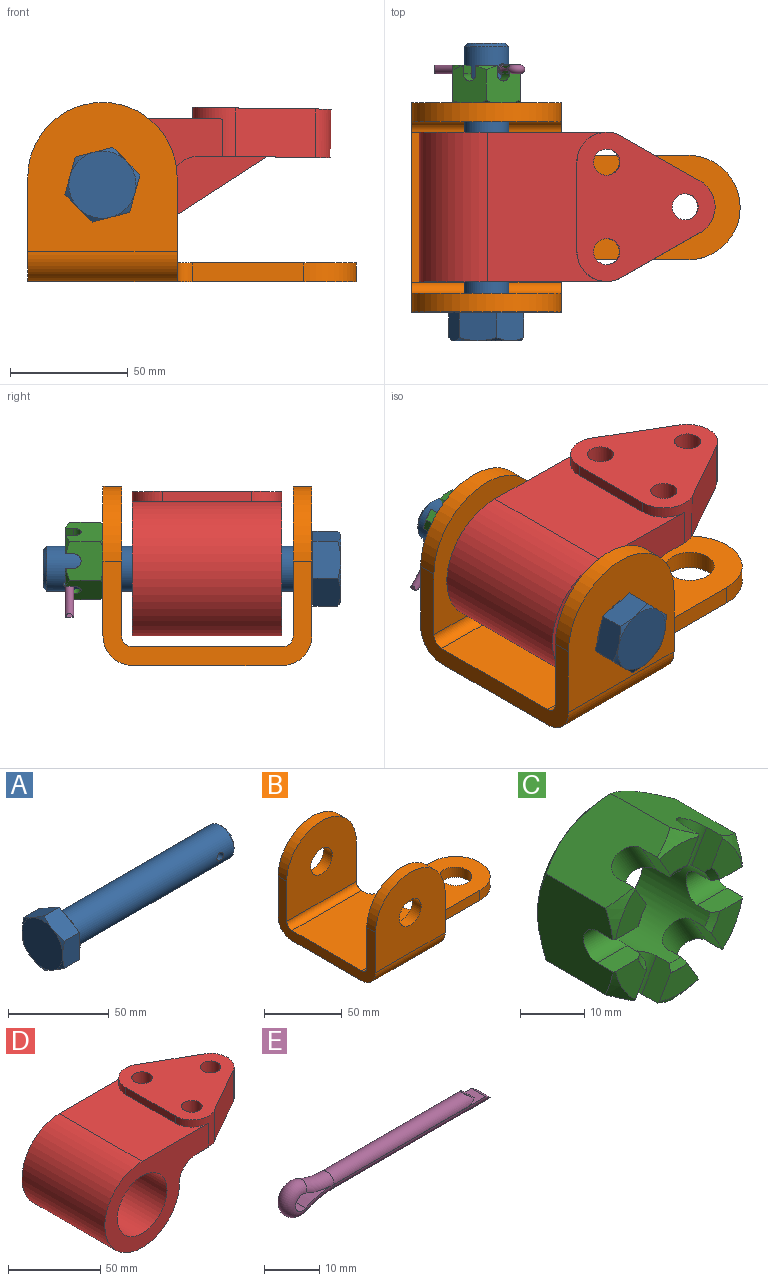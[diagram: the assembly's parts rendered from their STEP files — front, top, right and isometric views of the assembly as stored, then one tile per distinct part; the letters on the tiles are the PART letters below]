
ASSEMBLY  parts=5 mates=4
PART A: 26 faces, bbox 126.6x33x33 mm
  f0: plane 28.58x28.58mm, normal (1,0,0), area 325.1mm2, adj f10,f24
  f1: cylinder r=9.53mm len=112.28mm, axis (-1,0,0), area 6683.8mm2, adj f2,f24,f25
  f2: cone r=8.01mm half-angle=45deg, axis (-1,0,0), area 117.9mm2, adj f1,f3
  f3: plane 16.03x16.03mm, normal (1,0,0), area 201.7mm2, adj f2
  f4: plane 12.37x7.14mm, normal (1,0,0), area 11mm2, adj f10,f18,f23
  f5: plane 14.29x4.12mm, normal (1,0,0), area 11mm2, adj f10,f22,f23
  f6: plane 12.37x7.14mm, normal (1,0,0), area 11mm2, adj f10,f21,f22
  f7: plane 12.37x7.14mm, normal (1,0,0), area 11mm2, adj f10,f20,f21
  f8: plane 14.29x4.12mm, normal (1,0,0), area 11mm2, adj f10,f19,f20
  f9: plane 12.37x7.14mm, normal (1,0,0), area 11mm2, adj f10,f18,f19
  f10: cylinder r=14.29mm len=28.58mm, axis (-1,0,0), area 34.2mm2, adj f0,f4,f5,f6,f7,f8,f9
  f11: plane 28.58x28.58mm, normal (-1,0,0), area 641.3mm2, adj f12,f13,f14,f15,f16,f17
  f12: cone r=14.29mm half-angle=60deg, axis (1,0,0), area 12.7mm2, adj f11,f22,f23
  f13: cone r=14.29mm half-angle=60deg, axis (1,0,0), area 12.7mm2, adj f11,f21,f22
  f14: cone r=14.29mm half-angle=60deg, axis (1,0,0), area 12.7mm2, adj f11,f20,f21
  f15: cone r=14.29mm half-angle=60deg, axis (1,0,0), area 12.7mm2, adj f11,f19,f20
  f16: cone r=14.29mm half-angle=60deg, axis (1,0,0), area 12.7mm2, adj f11,f18,f23
  f17: cone r=14.29mm half-angle=60deg, axis (1,0,0), area 12.7mm2, adj f11,f18,f19
  f18: plane 16.51x11.89mm, normal (0,1,0), area 188.9mm2, adj f4,f9,f16,f17,f19,f23
  f19: plane 14.29x11.89mm, normal (0,0.5,-0.87), area 188.9mm2, adj f8,f9,f15,f17,f18,f20
  f20: plane 14.29x11.89mm, normal (0,-0.5,-0.87), area 188.9mm2, adj f7,f8,f14,f15,f19,f21
  f21: plane 16.51x11.89mm, normal (0,-1,0), area 188.9mm2, adj f6,f7,f13,f14,f20,f22
  f22: plane 14.29x11.89mm, normal (0,-0.5,0.87), area 188.9mm2, adj f5,f6,f12,f13,f21,f23
  f23: plane 14.29x11.89mm, normal (0,0.5,0.87), area 188.9mm2, adj f4,f5,f12,f16,f18,f22
  f24: torus R=10.03mm, axis (1,0,0), area 48.7mm2, adj f0,f1
  f25: cylinder r=2.38mm len=19.05mm, axis (0,-1,0), area 285mm2, adj f1
PART B: 24 faces, bbox 139.7x88.9x76.2 mm
  f0: plane 63.5x63.5mm, normal (0,-1,0), area 3290.3mm2, adj f5,f8,f16,f18,f23
  f1: plane 139.7x63.5mm, normal (0,0,1), area 6554.8mm2, adj f5,f6,f8,f9,f10,f11,f12,f13
  f2: plane 63.5x63.5mm, normal (0,1,0), area 3290.3mm2, adj f6,f8,f17,f19,f22
  f3: plane 63.5x63.5mm, normal (0,1,0), area 3290.3mm2, adj f5,f8,f16,f18,f21
  f4: plane 63.5x63.5mm, normal (0,-1,0), area 3290.3mm2, adj f6,f8,f17,f19,f20
  f5: plane 44.45x15.88mm, normal (1,0,0), area 386.1mm2, adj f0,f1,f3,f7,f12,f16,f21,f23
  f6: plane 44.45x15.88mm, normal (1,0,0), area 386.1mm2, adj f1,f2,f4,f7,f15,f17,f20,f22
  f7: plane 139.7x63.5mm, normal (0,0,-1), area 6554.8mm2, adj f5,f6,f8,f9,f10,f11,f12,f13
  f8: plane 88.9x44.45mm, normal (-1,0,0), area 1225.8mm2, adj f0,f1,f2,f3,f4,f7,f16,f17
  f9: plane 47.63x7.94mm, normal (0,-1,0), area 378mm2, adj f1,f7,f10,f15
  f10: cylinder r=22.23mm len=44.45mm, axis (0,0,-1), area 554.2mm2, adj f1,f7,f9,f11
  f11: plane 47.63x7.94mm, normal (0,1,0), area 378mm2, adj f1,f7,f10,f12
  f12: cylinder r=6.35mm len=7.94mm, axis (0,0,-1), area 79.2mm2, adj f1,f5,f7,f11
  f13: cylinder r=10.33mm len=20.65mm, axis (0,0,-1), area 514.9mm2, adj f1,f7
  f14: cylinder r=10.33mm len=20.65mm, axis (0,0,-1), area 514.9mm2, adj f1,f7
  f15: cylinder r=6.35mm len=7.94mm, axis (0,0,-1), area 79.2mm2, adj f1,f6,f7,f9
  f16: cylinder r=31.75mm len=63.5mm, axis (0,-1,0), area 791.7mm2, adj f0,f3,f5,f8
  f17: cylinder r=31.75mm len=63.5mm, axis (0,-1,0), area 791.7mm2, adj f2,f4,f6,f8
  f18: cylinder r=9.92mm len=19.85mm, axis (0,-1,0), area 494.9mm2, adj f0,f3
  f19: cylinder r=9.92mm len=19.85mm, axis (0,-1,0), area 494.9mm2, adj f2,f4
  f20: cylinder r=12.7mm len=63.5mm, axis (-1,0,0), area 1266.8mm2, adj f4,f6,f7,f8
  f21: cylinder r=12.7mm len=63.5mm, axis (-1,0,0), area 1266.8mm2, adj f3,f5,f7,f8
  f22: cylinder r=4.76mm len=63.5mm, axis (-1,0,0), area 475mm2, adj f1,f2,f6,f8
  f23: cylinder r=4.76mm len=63.5mm, axis (-1,0,0), area 475mm2, adj f0,f1,f5,f8
PART C: 64 faces, bbox 33x16.9x33 mm
  f0: cylinder r=8.33mm len=16.67mm, axis (0,-1,0), area 599.6mm2, adj f8,f9,f10,f11,f12,f13,f14,f15
  f1: plane 28.58x28.58mm, normal (0,1,0), area 356.3mm2, adj f32,f33,f34,f35,f36,f37,f51
  f2: plane 8.68x4.95mm, normal (0,-1,0), area 30mm2, adj f12,f16,f41,f48
  f3: plane 7.52x6.81mm, normal (0,-1,0), area 30mm2, adj f9,f13,f43,f49
  f4: plane 7.52x6.81mm, normal (0,-1,0), area 30mm2, adj f8,f18,f39,f44
  f5: plane 7.52x6.81mm, normal (0,-1,0), area 30mm2, adj f11,f15,f42,f46
  f6: plane 7.52x6.81mm, normal (0,-1,0), area 30mm2, adj f10,f17,f40,f47
  f7: plane 8.68x4.95mm, normal (0,-1,0), area 30mm2, adj f14,f19,f38,f45
  f8: plane 6.56x3.71mm, normal (0,0,-1), area 23.4mm2, adj f0,f4,f22,f26,f39,f44,f62,f63
  f9: plane 6.56x3.71mm, normal (0,0,1), area 23.4mm2, adj f0,f3,f22,f26,f43,f49,f52,f53
  f10: plane 6.56x3.71mm, normal (0,0,1), area 23.4mm2, adj f0,f6,f25,f27,f40,f47,f56,f57
  f11: plane 6.56x3.71mm, normal (0,0,-1), area 23.4mm2, adj f0,f5,f25,f27,f42,f46,f58,f59
  f12: plane 5.69x3.71mm, normal (0.87,0,0.5), area 23.4mm2, adj f0,f2,f23,f28,f41,f48,f54,f55
  f13: plane 5.69x3.71mm, normal (-0.87,0,-0.5), area 23.4mm2, adj f0,f3,f23,f28,f43,f49,f52,f53
  f14: plane 5.69x3.71mm, normal (-0.87,0,-0.5), area 23.4mm2, adj f0,f7,f20,f29,f38,f45,f60,f61
  f15: plane 5.69x3.71mm, normal (0.87,0,0.5), area 23.4mm2, adj f0,f5,f20,f29,f42,f46,f58,f59
  f16: plane 5.69x3.71mm, normal (-0.87,0,0.5), area 23.4mm2, adj f0,f2,f24,f30,f41,f48,f54,f55
  f17: plane 5.69x3.71mm, normal (0.87,0,-0.5), area 23.4mm2, adj f0,f6,f24,f30,f40,f47,f56,f57
  f18: plane 5.69x3.71mm, normal (-0.87,0,0.5), area 23.4mm2, adj f0,f4,f21,f31,f39,f44,f62,f63
  f19: plane 5.69x3.71mm, normal (0.87,0,-0.5), area 23.4mm2, adj f0,f7,f21,f31,f38,f45,f60,f61
  f20: plane 16.62x14.29mm, normal (-0.5,0,0.87), area 220.6mm2, adj f14,f15,f21,f25,f29,f32,f33,f38
  f21: plane 16.62x14.29mm, normal (0.5,0,0.87), area 220.6mm2, adj f18,f19,f20,f22,f31,f33,f34,f38
  f22: plane 16.63x16.51mm, normal (1,0,0), area 220.6mm2, adj f8,f9,f21,f23,f26,f34,f35,f39
  f23: plane 16.62x14.29mm, normal (0.5,0,-0.87), area 220.6mm2, adj f12,f13,f22,f24,f28,f35,f36,f41
  f24: plane 16.62x14.29mm, normal (-0.5,0,-0.87), area 220.6mm2, adj f16,f17,f23,f25,f30,f36,f37,f40
  f25: plane 16.63x16.51mm, normal (-1,0,0), area 220.6mm2, adj f10,f11,f20,f24,f27,f32,f37,f40
  f26: cylinder r=3.05mm len=6.53mm, axis (1,0,0), area 59.8mm2, adj f0,f8,f9,f22
  f27: cylinder r=3.05mm len=6.53mm, axis (1,0,0), area 59.8mm2, adj f0,f10,f11,f25
  f28: cylinder r=3.05mm len=8.7mm, axis (-0.5,0,0.87), area 59.8mm2, adj f0,f12,f13,f23
  f29: cylinder r=3.05mm len=8.7mm, axis (-0.5,0,0.87), area 59.8mm2, adj f0,f14,f15,f20
  f30: cylinder r=3.05mm len=8.7mm, axis (0.5,0,0.87), area 59.8mm2, adj f0,f16,f17,f24
  f31: cylinder r=3.05mm len=8.7mm, axis (0.5,0,0.87), area 59.8mm2, adj f0,f18,f19,f21
  f32: cone r=14.29mm half-angle=49.2deg, axis (0,-1,0), area 14.5mm2, adj f1,f20,f25
  f33: cone r=14.29mm half-angle=49.2deg, axis (0,-1,0), area 14.5mm2, adj f1,f20,f21
  f34: cone r=14.29mm half-angle=49.2deg, axis (0,-1,0), area 14.5mm2, adj f1,f21,f22
  f35: cone r=14.29mm half-angle=49.2deg, axis (0,-1,0), area 14.5mm2, adj f1,f22,f23
  f36: cone r=14.29mm half-angle=49.2deg, axis (0,-1,0), area 14.5mm2, adj f1,f23,f24
  f37: cone r=14.29mm half-angle=49.2deg, axis (0,-1,0), area 14.5mm2, adj f1,f24,f25
  f38: cone r=14.29mm half-angle=49.2deg, axis (0,1,0), area 13.6mm2, adj f7,f14,f19,f20,f21
  f39: cone r=14.29mm half-angle=49.2deg, axis (0,1,0), area 13.6mm2, adj f4,f8,f18,f21,f22
  f40: cone r=14.29mm half-angle=49.2deg, axis (0,1,0), area 13.6mm2, adj f6,f10,f17,f24,f25
  f41: cone r=14.29mm half-angle=49.2deg, axis (0,1,0), area 13.6mm2, adj f2,f12,f16,f23,f24
  f42: cone r=14.29mm half-angle=49.2deg, axis (0,1,0), area 13.6mm2, adj f5,f11,f15,f20,f25
  f43: cone r=14.29mm half-angle=49.2deg, axis (0,1,0), area 13.6mm2, adj f3,f9,f13,f22,f23
  f44: cone r=8.21mm half-angle=55deg, axis (0,-1,0), area 0.1mm2, adj f4,f8,f18,f63
  f45: cone r=8.21mm half-angle=55deg, axis (0,-1,0), area 0.1mm2, adj f7,f14,f19,f60
  f46: cone r=8.21mm half-angle=55deg, axis (0,-1,0), area 0.1mm2, adj f5,f11,f15,f58
  f47: cone r=8.21mm half-angle=55deg, axis (0,-1,0), area 0.1mm2, adj f6,f10,f17,f56
  f48: cone r=8.21mm half-angle=55deg, axis (0,-1,0), area 0.1mm2, adj f2,f12,f16,f54
  f49: cone r=8.21mm half-angle=55deg, axis (0,-1,0), area 0.1mm2, adj f3,f9,f13,f52
  f50: cone r=9.53mm half-angle=55deg, axis (0,1,0), area 81.6mm2, adj f0,f51
  f51: cylinder r=9.53mm len=19.05mm, axis (0,-1,0), area 1.5mm2, adj f1,f50
  f52: cone r=9.53mm half-angle=55deg, axis (0,1,0), area 0.1mm2, adj f9,f13,f49,f53
  f53: cone r=8.33mm half-angle=55deg, axis (0,-1,0), area 4.5mm2, adj f0,f9,f13,f52
  f54: cone r=9.53mm half-angle=55deg, axis (0,1,0), area 0.1mm2, adj f12,f16,f48,f55
  f55: cone r=8.33mm half-angle=55deg, axis (0,-1,0), area 4.5mm2, adj f0,f12,f16,f54
  f56: cone r=9.53mm half-angle=55deg, axis (0,1,0), area 0.1mm2, adj f10,f17,f47,f57
  f57: cone r=8.33mm half-angle=55deg, axis (0,-1,0), area 4.5mm2, adj f0,f10,f17,f56
  f58: cone r=9.53mm half-angle=55deg, axis (0,1,0), area 0.1mm2, adj f11,f15,f46,f59
  f59: cone r=8.33mm half-angle=55deg, axis (0,-1,0), area 4.5mm2, adj f0,f11,f15,f58
  f60: cone r=9.53mm half-angle=55deg, axis (0,1,0), area 0.1mm2, adj f14,f19,f45,f61
  f61: cone r=8.33mm half-angle=55deg, axis (0,-1,0), area 4.5mm2, adj f0,f14,f19,f60
  f62: cone r=8.33mm half-angle=55deg, axis (0,-1,0), area 4.5mm2, adj f0,f8,f18,f63
  f63: cone r=9.53mm half-angle=55deg, axis (0,1,0), area 0.1mm2, adj f8,f18,f44,f62
PART D: 21 faces, bbox 125.4x63.5x61.9 mm
  f0: plane 63.5x55.58mm, normal (0,0,-1), area 1858.5mm2, adj f2,f4,f5,f9,f10,f11,f12,f13
  f1: cylinder r=28.57mm len=63.5mm, axis (0,1,0), area 8301mm2, adj f2,f4,f5,f7,f9,f18,f19,f20
  f2: cylinder r=12.7mm len=26.19mm, axis (0,1,0), area 522.4mm2, adj f0,f1,f5,f20
  f3: plane 63.5x58.75mm, normal (0,0,1), area 2308.8mm2, adj f6,f10,f11,f12,f13,f14,f15,f16
  f4: plane 79.38x57.15mm, normal (0,-1,0), area 1987.8mm2, adj f0,f1,f7,f8,f9,f14
  f5: plane 79.38x57.15mm, normal (0,1,0), area 1987.8mm2, adj f0,f1,f2,f7,f8,f13
  f6: plane 38.1x4.78mm, normal (-1,0,0), area 181.9mm2, adj f3,f7,f13,f14
  f7: plane 63.5x50.8mm, normal (0,0,1), area 2488.6mm2, adj f1,f4,f5,f6,f13,f14
  f8: cylinder r=19.05mm len=63.5mm, axis (0,1,0), area 7600.6mm2, adj f4,f5
  f9: cylinder r=12.7mm len=26.19mm, axis (0,1,0), area 522.4mm2, adj f0,f1,f4,f19
  f10: cylinder r=5.56mm len=20.65mm, axis (0,0,1), area 721.7mm2, adj f0,f3
  f11: cylinder r=5.56mm len=20.65mm, axis (0,0,1), area 721.7mm2, adj f0,f3
  f12: cylinder r=5.56mm len=20.65mm, axis (0,0,1), area 721.7mm2, adj f0,f3
  f13: cylinder r=12.7mm len=20.65mm, axis (0,0,1), area 214.2mm2, adj f0,f3,f5,f6,f7,f15
  f14: cylinder r=12.7mm len=20.65mm, axis (0,0,1), area 214.2mm2, adj f0,f3,f4,f6,f7,f17
  f15: plane 34.08x20.65mm, normal (0.5,0.87,0), area 810.1mm2, adj f0,f3,f13,f16
  f16: cylinder r=12.7mm len=22.06mm, axis (0,0,1), area 552.1mm2, adj f0,f3,f15,f17
  f17: plane 34.08x20.65mm, normal (0.5,-0.87,0), area 810.1mm2, adj f0,f3,f14,f16
  f18: plane 49.64x32.91mm, normal (0.55,0,-0.83), area 662.6mm2, adj f0,f1,f19,f20
  f19: plane 49.64x32.91mm, normal (0,-1,0), area 559.4mm2, adj f0,f1,f9,f18
  f20: plane 49.64x32.91mm, normal (0,1,0), area 559.4mm2, adj f0,f1,f2,f18
PART E: 14 faces, bbox 52x3.7x8 mm
  f0: plane 38.67x3.7mm, normal (0,0,1), area 143.1mm2, adj f1,f2,f13
  f1: cylinder r=1.85mm len=40mm, axis (1,0,0), area 227.7mm2, adj f0,f3,f12,f13
  f2: cylinder r=16.37mm len=7.19mm, axis (0,1,0), area 27.5mm2, adj f0,f3,f4
  f3: torus R=16.37mm, axis (0,1,0), area 40.1mm2, adj f1,f2,f5
  f4: cylinder r=1.85mm len=3.7mm, axis (0,-1,0), area 27.8mm2, adj f2,f5,f6
  f5: torus R=1.85mm, axis (0,-1,0), area 71.2mm2, adj f3,f4,f7
  f6: cylinder r=16.37mm len=7.19mm, axis (0,1,0), area 27.5mm2, adj f4,f7,f9
  f7: torus R=16.37mm, axis (0,1,0), area 40.1mm2, adj f5,f6,f8
  f8: cylinder r=1.85mm len=36mm, axis (1,0,0), area 204.5mm2, adj f7,f9,f10,f11
  f9: plane 34.67x3.7mm, normal (0,0,-1), area 128.3mm2, adj f6,f8,f10
  f10: plane 3.7x1.33mm, normal (0.57,0,-0.82), area 5.7mm2, adj f8,f9,f11
  f11: plane 3.2x1.31mm, normal (0.58,0,0.82), area 3.6mm2, adj f8,f10
  f12: plane 3.2x1.31mm, normal (0.58,0,-0.82), area 3.6mm2, adj f1,f13
  f13: plane 3.7x1.33mm, normal (0.57,0,0.82), area 5.7mm2, adj f0,f1,f12
PLACE A rot(axis=(-0.35,-0.35,0.87),98.2deg) t=(-1.25,-80.18,-10.24)mm
PLACE B t=(-33,-23.47,-51.45)mm fixed
PLACE C rot(axis=(1,0,0),180deg) t=(-1.25,37.01,-7)mm
PLACE D rot(axis=(0,1,0),0.7deg) t=(-1.25,-23.29,-10.24)mm
PLACE E rot(axis=(0,1,0),135.5deg) t=(11.34,35.27,2.12)mm
MATE revolute E.f8 <-> A.f25  axis (-0.71,0,-0.7) through (5.63,35.27,-3.48)mm
MATE revolute A.f1 <-> B.f4  axis (0,1,0) through (-1.25,-67.92,-10.24)mm
MATE cylindrical A.f1 <-> D.f1  axis (0,-1,0) through (-1.25,-11.27,-10.24)mm
MATE revolute C.f0 <-> B.f16  axis (0,1,0) through (-1.25,20.98,-7)mm
